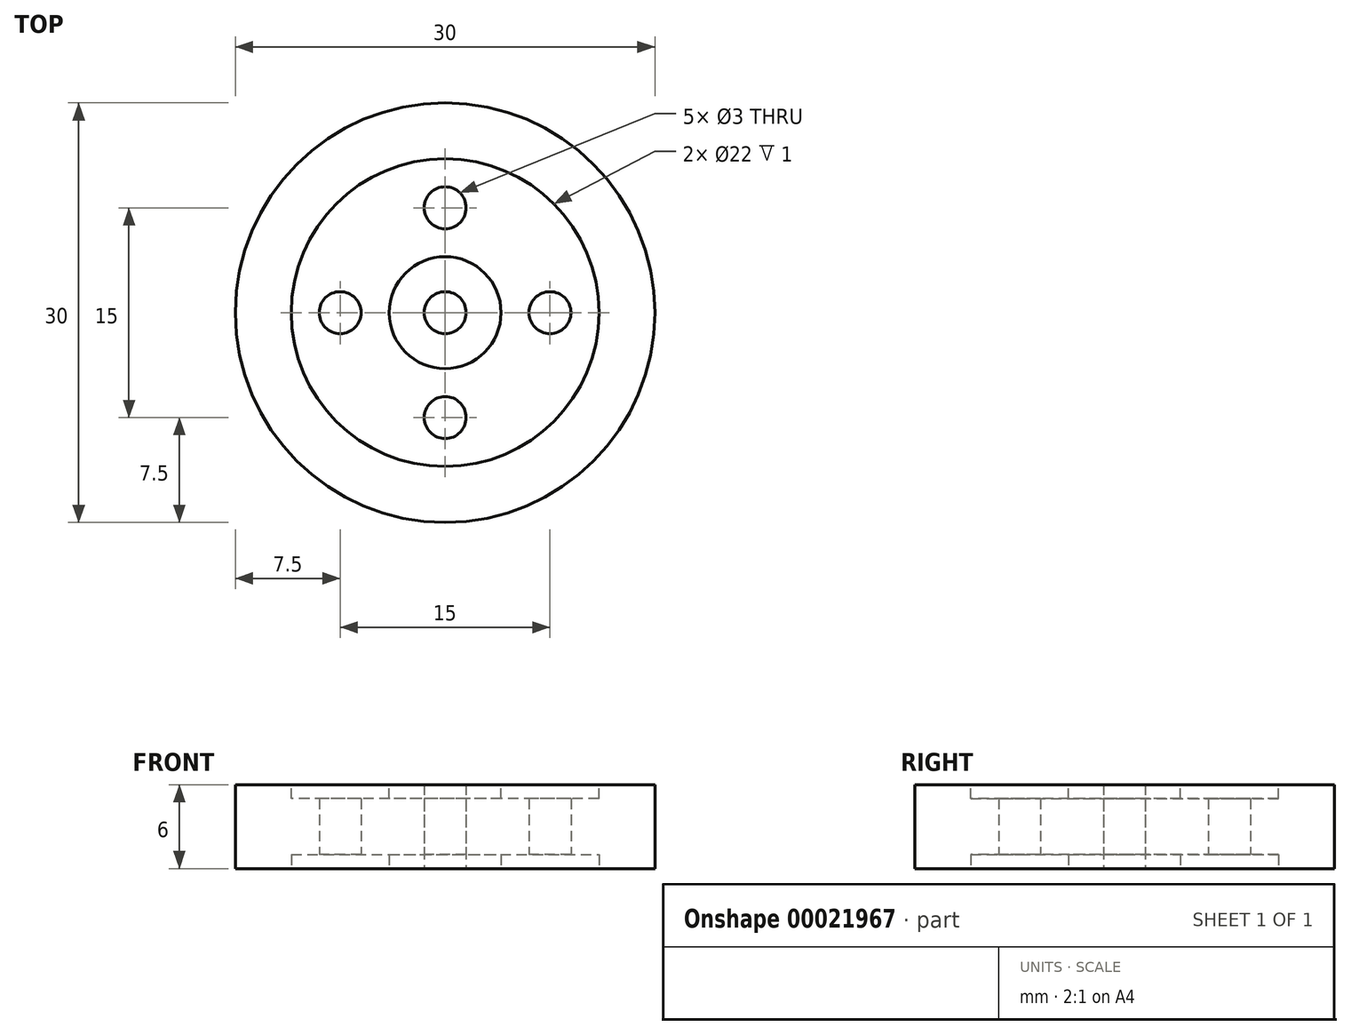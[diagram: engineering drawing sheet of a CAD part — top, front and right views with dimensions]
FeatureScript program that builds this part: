
annotation { "Feature Type Name" : "Feature", "Feature Type Description" : "" }
export const myFeature = defineFeature(function(context is Context, id is Id, definition is map)
    precondition{}
    {
        {
            var Q0;
            Q0=qCreatedBy(makeId("Top.planeOp"),FACE);
            var sketch = newSketch(context, id + "F0", { "sketchPlane" : qUnion([Q0])});
            skCircle(sketch, "E0", {"center": v(0, 0) * mm, "radius": 15 * mm});
            skCircle(sketch, "E1", {"center": v(0, 7.5) * mm, "radius": 1.5 * mm});
            skCircle(sketch, "E2.1.0", {"center": v(-7.5, 0) * mm, "radius": 1.5 * mm});
            skCircle(sketch, "E2.2.0", {"center": v(0, -7.5) * mm, "radius": 1.5 * mm});
            skCircle(sketch, "E3.1.3.0", {"center": v(7.5, 0) * mm, "radius": 1.5 * mm});
            skCircle(sketch, "E4", {"center": v(0, 0) * mm, "radius": 1.5 * mm});
            skSolve(sketch);
        }
        {
            var Q0;
            Q0=makeQuery(id+"F0.imprint","IMPRINT",FACE,{"disambiguationData":[TD([[makeQuery(id+"F0.imprint","IMPRINT",EDGE,{"derivedFrom":sQuery(id+"F0.wireOp",EDGE,"E0")}),1.0]])]});
            extrude(context, id + "F1", {"entities" : qUnion([Q0]), "depth" : 6 * mm});
        }
        {
            var Q0;
            Q0=makeQuery(id+"F1.opExtrude","CAP_FACE",FACE,{"disambiguationData":[OSD([sQuery(id+"F0.wireOp",EDGE,"E0"),sQuery(id+"F0.wireOp",EDGE,"E1"),sQuery(id+"F0.wireOp",EDGE,"E2.1.0"),sQuery(id+"F0.wireOp",EDGE,"E2.2.0"),sQuery(id+"F0.wireOp",EDGE,"E3.1.3.0")])],"isStart":false});
            var sketch = newSketch(context, id + "F2", { "sketchPlane" : qUnion([Q0])});
            skCircle(sketch, "E5", {"center": v(0, 0) * mm, "radius": 11 * mm});
            skCircle(sketch, "E6", {"center": v(0, 0) * mm, "radius": 4 * mm});
            skSolve(sketch);
        }
        {
            var Q0;
            Q0=makeQuery(id+"F2.imprint","IMPRINT",FACE,{"disambiguationData":[TD([[makeQuery(id+"F2.imprint","IMPRINT",EDGE,{"derivedFrom":sQuery(id+"F2.wireOp",EDGE,"E5")}),1.0]])]});
            extrude(context, id + "F3", {"entities" : qUnion([Q0]), "operationType" : NewBodyOperationType.REMOVE, "oppositeDirection" : true, "depth" : 1 * mm});
        }
        {
            var Q0;
            Q0=makeQuery(id+"F1.opExtrude","CAP_FACE",FACE,{"disambiguationData":[OSD([sQuery(id+"F0.wireOp",EDGE,"E0"),sQuery(id+"F0.wireOp",EDGE,"E1"),sQuery(id+"F0.wireOp",EDGE,"E2.1.0"),sQuery(id+"F0.wireOp",EDGE,"E2.2.0"),sQuery(id+"F0.wireOp",EDGE,"E3.1.3.0"),sQuery(id+"F0.wireOp",EDGE,"E4")])],"isStart":true});
            var sketch = newSketch(context, id + "F4", { "sketchPlane" : qUnion([Q0])});
            skCircle(sketch, "E7", {"center": v(0, 0) * mm, "radius": 4 * mm});
            skCircle(sketch, "E8", {"center": v(0, 0) * mm, "radius": 11 * mm});
            skSolve(sketch);
        }
        {
            var Q0;
            Q0=makeQuery(id+"F4.imprint","IMPRINT",FACE,{"disambiguationData":[TD([[makeQuery(id+"F4.imprint","IMPRINT",EDGE,{"derivedFrom":sQuery(id+"F4.wireOp",EDGE,"E7")}),-1.0]])]});
            extrude(context, id + "F5", {"entities" : qUnion([Q0]), "operationType" : NewBodyOperationType.REMOVE, "oppositeDirection" : true, "depth" : 1 * mm});
        }
    });
